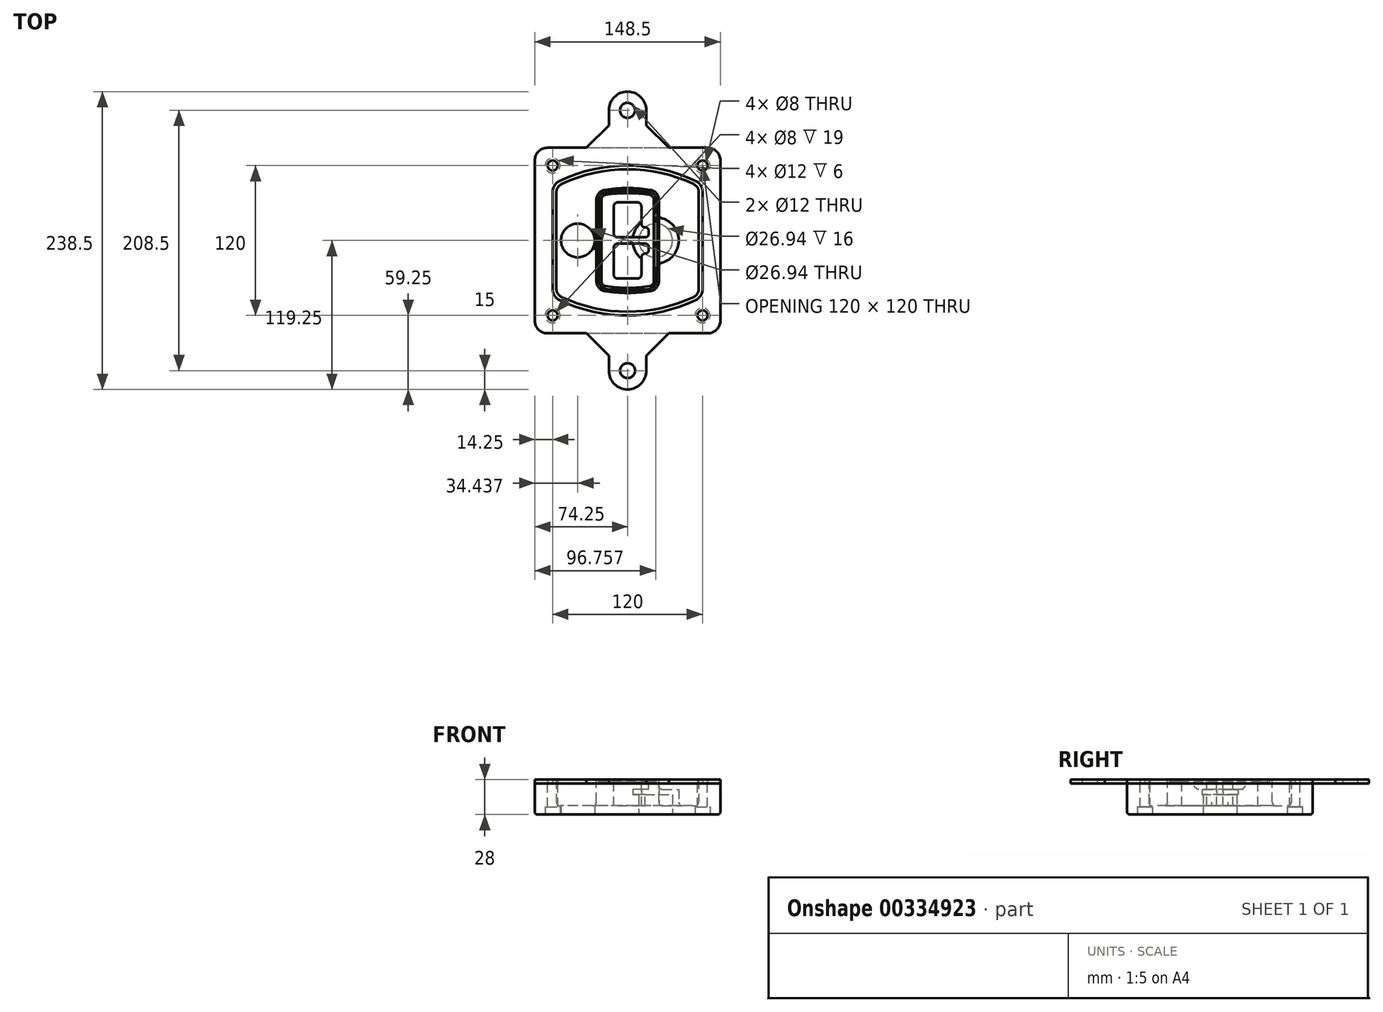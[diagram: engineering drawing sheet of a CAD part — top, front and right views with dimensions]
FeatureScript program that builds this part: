
annotation { "Feature Type Name" : "Feature", "Feature Type Description" : "" }
export const myFeature = defineFeature(function(context is Context, id is Id, definition is map)
    precondition{}
    {
        {
            var Q0;
            Q0=qCreatedBy(makeId("Top.planeOp"),FACE);
            var sketch = newSketch(context, id + "F0", { "sketchPlane" : qUnion([Q0])});
            skPoint(sketch, "E0.rect.middle", {"position": v(0, 0) * mm});
            skLineSegment(sketch, "E1.bottom", {"start": v(-64.25, -74.25) * mm, "end": v(64.25, -74.25) * mm});
            skLineSegment(sketch, "E1.top", {"start": v(-64.25, 74.25) * mm, "end": v(64.25, 74.25) * mm});
            skLineSegment(sketch, "E1.left", {"start": v(-74.25, -64.25) * mm, "end": v(-74.25, 64.25) * mm});
            skLineSegment(sketch, "E1.right", {"start": v(74.25, -64.25) * mm, "end": v(74.25, 64.25) * mm});
            skLineSegment(sketch, "E2", {"start": v(-74.25, 74.25) * mm, "end": v(74.25, -74.25) * mm, "construction": true});
            skLineSegment(sketch, "E3", {"start": v(74.25, 74.25) * mm, "end": v(-74.25, -74.25) * mm, "construction": true});
            skCircle(sketch, "E4", {"center": v(-60, 60) * mm, "radius": 4 * mm});
            skCircle(sketch, "E5", {"center": v(60, 60) * mm, "radius": 4 * mm});
            skCircle(sketch, "E6", {"center": v(60, -60) * mm, "radius": 4 * mm});
            skCircle(sketch, "E7", {"center": v(-60, -60) * mm, "radius": 4 * mm});
            skLineSegment(sketch, "E8", {"start": v(-60, 60) * mm, "end": v(60, 60) * mm, "construction": true});
            skLineSegment(sketch, "E9", {"start": v(60, 60) * mm, "end": v(60, -60) * mm, "construction": true});
            skLineSegment(sketch, "E10", {"start": v(60, -60) * mm, "end": v(-60, -60) * mm, "construction": true});
            skLineSegment(sketch, "E11", {"start": v(-60, -60) * mm, "end": v(-60, 60) * mm, "construction": true});
            skLineSegment(sketch, "E12", {"start": v(-60, 38.83) * mm, "end": v(-60, -38.83) * mm});
            skLineSegment(sketch, "E13", {"start": v(60, 38.83) * mm, "end": v(60, -38.83) * mm});
            skArc(sketch, "E14", {"start": v(54.26, 47.88) * mm, "mid": v(0, 60) * mm, "end": v(-54.26, 47.88) * mm});
            skArc(sketch, "E15", {"start": v(-54.26, -47.88) * mm, "mid": v(0, -60) * mm, "end": v(54.26, -47.88) * mm});
            skLineSegment(sketch, "E16", {"start": v(-60, 0) * mm, "end": v(60, 0) * mm, "construction": true});
            skPoint(sketch, "E17.visualSharp", {"position": v(-60, -45) * mm});
            skArc(sketch, "E17.filletArc", {"start": v(-60, -38.83) * mm, "mid": v(-58.44, -44.2) * mm, "end": v(-54.26, -47.88) * mm});
            skPoint(sketch, "E18.visualSharp", {"position": v(-60, 45) * mm});
            skArc(sketch, "E18.filletArc", {"start": v(-54.26, 47.88) * mm, "mid": v(-58.44, 44.2) * mm, "end": v(-60, 38.83) * mm});
            skPoint(sketch, "E19.visualSharp", {"position": v(60, 45) * mm});
            skArc(sketch, "E19.filletArc", {"start": v(60, 38.83) * mm, "mid": v(58.44, 44.2) * mm, "end": v(54.26, 47.88) * mm});
            skPoint(sketch, "E20.visualSharp", {"position": v(60, -45) * mm});
            skArc(sketch, "E20.filletArc", {"start": v(54.26, -47.88) * mm, "mid": v(58.44, -44.2) * mm, "end": v(60, -38.83) * mm});
            skPoint(sketch, "E21.visualSharp", {"position": v(-74.25, 74.25) * mm});
            skArc(sketch, "E21.filletArc", {"start": v(-64.25, 74.25) * mm, "mid": v(-71.32, 71.32) * mm, "end": v(-74.25, 64.25) * mm});
            skPoint(sketch, "E22.visualSharp", {"position": v(74.25, 74.25) * mm});
            skArc(sketch, "E22.filletArc", {"start": v(74.25, 64.25) * mm, "mid": v(71.32, 71.32) * mm, "end": v(64.25, 74.25) * mm});
            skPoint(sketch, "E23.visualSharp", {"position": v(74.25, -74.25) * mm});
            skArc(sketch, "E23.filletArc", {"start": v(64.25, -74.25) * mm, "mid": v(71.32, -71.32) * mm, "end": v(74.25, -64.25) * mm});
            skPoint(sketch, "E24.visualSharp", {"position": v(-74.25, -74.25) * mm});
            skArc(sketch, "E24.filletArc", {"start": v(-74.25, -64.25) * mm, "mid": v(-71.32, -71.32) * mm, "end": v(-64.25, -74.25) * mm});
            skArc(sketch, "E25.0", {"start": v(57, 38.83) * mm, "mid": v(55.9, 42.58) * mm, "end": v(52.98, 45.17) * mm});
            skLineSegment(sketch, "E25.1", {"start": v(57, 38.83) * mm, "end": v(57, -38.83) * mm});
            skArc(sketch, "E25.2", {"start": v(52.98, -45.17) * mm, "mid": v(55.9, -42.58) * mm, "end": v(57, -38.83) * mm});
            skArc(sketch, "E25.3", {"start": v(-52.98, -45.17) * mm, "mid": v(0, -57) * mm, "end": v(52.98, -45.17) * mm});
            skArc(sketch, "E25.4", {"start": v(-57, -38.83) * mm, "mid": v(-55.9, -42.58) * mm, "end": v(-52.98, -45.17) * mm});
            skArc(sketch, "E25.5", {"start": v(52.98, 45.17) * mm, "mid": v(0, 57) * mm, "end": v(-52.98, 45.17) * mm});
            skLineSegment(sketch, "E25.6", {"start": v(-57, 38.83) * mm, "end": v(-57, -38.83) * mm});
            skArc(sketch, "E25.7", {"start": v(-52.98, 45.17) * mm, "mid": v(-55.9, 42.58) * mm, "end": v(-57, 38.83) * mm});
            skArc(sketch, "E26.0", {"start": v(-55.96, 51.5) * mm, "mid": v(-61.82, 46.33) * mm, "end": v(-64, 38.83) * mm});
            skArc(sketch, "E26.1", {"start": v(55.96, 51.5) * mm, "mid": v(0, 64) * mm, "end": v(-55.96, 51.5) * mm});
            skArc(sketch, "E26.2", {"start": v(64, 38.83) * mm, "mid": v(61.82, 46.33) * mm, "end": v(55.96, 51.5) * mm});
            skLineSegment(sketch, "E26.3", {"start": v(64, 38.83) * mm, "end": v(64, -38.83) * mm});
            skArc(sketch, "E26.4", {"start": v(55.96, -51.5) * mm, "mid": v(61.82, -46.33) * mm, "end": v(64, -38.83) * mm});
            skLineSegment(sketch, "E26.5", {"start": v(-64, 38.83) * mm, "end": v(-64, -38.83) * mm});
            skArc(sketch, "E26.6", {"start": v(-55.96, -51.5) * mm, "mid": v(0, -64) * mm, "end": v(55.96, -51.5) * mm});
            skArc(sketch, "E26.7", {"start": v(-64, -38.83) * mm, "mid": v(-61.82, -46.33) * mm, "end": v(-55.96, -51.5) * mm});
            skSolve(sketch);
        }
        {
            var Q0;
            Q0=makeQuery(id+"F0.imprint","IMPRINT",FACE,{"disambiguationData":[TD([[makeQuery(id+"F0.imprint","IMPRINT",EDGE,{"derivedFrom":sQuery(id+"F0.wireOp",EDGE,"E1.bottom")}),1.0]])]});
            var Q1;
            Q1=makeQuery(id+"F0.imprint","IMPRINT",FACE,{"disambiguationData":[TD([[makeQuery(id+"F0.imprint","IMPRINT",EDGE,{"derivedFrom":sQuery(id+"F0.wireOp",EDGE,"E12")}),1.0]])]});
            var Q2;
            Q2=makeQuery(id+"F0.imprint","IMPRINT",FACE,{"disambiguationData":[TD([[makeQuery(id+"F0.imprint","IMPRINT",EDGE,{"derivedFrom":sQuery(id+"F0.wireOp",EDGE,"E25.0")}),1.0]])]});
            var Q3;
            Q3=makeQuery(id+"F0.imprint","IMPRINT",FACE,{"disambiguationData":[TD([[makeQuery(id+"F0.imprint","IMPRINT",EDGE,{"derivedFrom":sQuery(id+"F0.wireOp",EDGE,"E12")}),-1.0]])]});
            extrude(context, id + "F1", {"entities" : qUnion([Q0, Q1, Q2, Q3]), "oppositeDirection" : true, "depth" : 25 * mm});
        }
        {
            var Q0;
            Q0=makeQuery(id+"F0.imprint","IMPRINT",FACE,{"disambiguationData":[TD([[makeQuery(id+"F0.imprint","IMPRINT",EDGE,{"derivedFrom":sQuery(id+"F0.wireOp",EDGE,"E12")}),1.0]])]});
            extrude(context, id + "F2", {"entities" : qUnion([Q0]), "operationType" : NewBodyOperationType.ADD, "depth" : 3 * mm});
        }
        {
            var Q0;
            Q0=makeQuery(id+"F0.imprint","IMPRINT",FACE,{"disambiguationData":[TD([[makeQuery(id+"F0.imprint","IMPRINT",EDGE,{"derivedFrom":sQuery(id+"F0.wireOp",EDGE,"E25.0")}),1.0]])]});
            extrude(context, id + "F3", {"entities" : qUnion([Q0]), "operationType" : NewBodyOperationType.REMOVE, "oppositeDirection" : true, "depth" : 18 * mm});
        }
        {
            var Q0;
            Q0=makeQuery(id+"F2.opExtrude","CAP_FACE",FACE,{"disambiguationData":[OSD([sQuery(id+"F0.wireOp",EDGE,"E12"),sQuery(id+"F0.wireOp",EDGE,"E13"),sQuery(id+"F0.wireOp",EDGE,"E14"),sQuery(id+"F0.wireOp",EDGE,"E15"),sQuery(id+"F0.wireOp",EDGE,"E17.filletArc"),sQuery(id+"F0.wireOp",EDGE,"E18.filletArc"),sQuery(id+"F0.wireOp",EDGE,"E19.filletArc"),sQuery(id+"F0.wireOp",EDGE,"E20.filletArc"),sQuery(id+"F0.wireOp",EDGE,"E25.0"),sQuery(id+"F0.wireOp",EDGE,"E25.1"),sQuery(id+"F0.wireOp",EDGE,"E25.2"),sQuery(id+"F0.wireOp",EDGE,"E25.3"),sQuery(id+"F0.wireOp",EDGE,"E25.4"),sQuery(id+"F0.wireOp",EDGE,"E25.5"),sQuery(id+"F0.wireOp",EDGE,"E25.6"),sQuery(id+"F0.wireOp",EDGE,"E25.7")])],"isStart":false});
            var sketch = newSketch(context, id + "F4", { "sketchPlane" : qUnion([Q0])});
            skArc(sketch, "E27.0", {"start": v(-18.34, -40.45) * mm, "mid": v(0, -42) * mm, "end": v(18.34, -40.45) * mm});
            skArc(sketch, "E28.0", {"start": v(18.34, 40.45) * mm, "mid": v(0, 42) * mm, "end": v(-18.34, 40.45) * mm});
            skLineSegment(sketch, "E29", {"start": v(-25, 32.57) * mm, "end": v(-25, -32.57) * mm});
            skLineSegment(sketch, "E30", {"start": v(25, 32.57) * mm, "end": v(25, -32.57) * mm});
            skLineSegment(sketch, "E31", {"start": v(-25, 39.1) * mm, "end": v(25, 39.1) * mm, "construction": true});
            skLineSegment(sketch, "E32", {"start": v(-25, -39.1) * mm, "end": v(25, -39.1) * mm, "construction": true});
            skPoint(sketch, "E33.visualSharp", {"position": v(-25, 39.1) * mm});
            skArc(sketch, "E33.filletArc", {"start": v(-18.34, 40.45) * mm, "mid": v(-23.11, 37.73) * mm, "end": v(-25, 32.57) * mm});
            skPoint(sketch, "E34.visualSharp", {"position": v(25, 39.1) * mm});
            skArc(sketch, "E34.filletArc", {"start": v(25, 32.57) * mm, "mid": v(23.11, 37.73) * mm, "end": v(18.34, 40.45) * mm});
            skPoint(sketch, "E35.visualSharp", {"position": v(25, -39.1) * mm});
            skArc(sketch, "E35.filletArc", {"start": v(18.34, -40.45) * mm, "mid": v(23.11, -37.73) * mm, "end": v(25, -32.57) * mm});
            skPoint(sketch, "E36.visualSharp", {"position": v(-25, -39.1) * mm});
            skArc(sketch, "E36.filletArc", {"start": v(-25, -32.57) * mm, "mid": v(-23.11, -37.73) * mm, "end": v(-18.34, -40.45) * mm});
            skArc(sketch, "E37.0", {"start": v(52.98, 45.17) * mm, "mid": v(0, 57) * mm, "end": v(-52.98, 45.17) * mm});
            skArc(sketch, "E37.1", {"start": v(-52.98, 45.17) * mm, "mid": v(-55.9, 42.58) * mm, "end": v(-57, 38.83) * mm});
            skLineSegment(sketch, "E37.2", {"start": v(-57, 38.83) * mm, "end": v(-57, -38.83) * mm});
            skArc(sketch, "E37.3", {"start": v(-57, -38.83) * mm, "mid": v(-55.9, -42.58) * mm, "end": v(-52.98, -45.17) * mm});
            skArc(sketch, "E37.4", {"start": v(-52.98, -45.17) * mm, "mid": v(0, -57) * mm, "end": v(52.98, -45.17) * mm});
            skArc(sketch, "E37.5", {"start": v(52.98, -45.17) * mm, "mid": v(55.9, -42.58) * mm, "end": v(57, -38.83) * mm});
            skLineSegment(sketch, "E37.6", {"start": v(57, 38.83) * mm, "end": v(57, -38.83) * mm});
            skArc(sketch, "E37.7", {"start": v(57, 38.83) * mm, "mid": v(55.9, 42.58) * mm, "end": v(52.98, 45.17) * mm});
            skLineSegment(sketch, "E38.0", {"start": v(23, 32.57) * mm, "end": v(23, -32.57) * mm});
            skArc(sketch, "E38.1", {"start": v(18, -38.48) * mm, "mid": v(21.58, -36.44) * mm, "end": v(23, -32.57) * mm});
            skArc(sketch, "E38.2", {"start": v(-18, -38.48) * mm, "mid": v(0, -40) * mm, "end": v(18, -38.48) * mm});
            skArc(sketch, "E38.3", {"start": v(-23, -32.57) * mm, "mid": v(-21.58, -36.44) * mm, "end": v(-18, -38.48) * mm});
            skLineSegment(sketch, "E38.4", {"start": v(-23, 32.57) * mm, "end": v(-23, -32.57) * mm});
            skArc(sketch, "E38.5", {"start": v(23, 32.57) * mm, "mid": v(21.58, 36.44) * mm, "end": v(18, 38.48) * mm});
            skArc(sketch, "E38.6", {"start": v(-18, 38.48) * mm, "mid": v(-21.58, 36.44) * mm, "end": v(-23, 32.57) * mm});
            skArc(sketch, "E38.7", {"start": v(18, 38.48) * mm, "mid": v(0, 40) * mm, "end": v(-18, 38.48) * mm});
            skArc(sketch, "E39.0", {"start": v(21, 32.57) * mm, "mid": v(20.06, 35.15) * mm, "end": v(17.67, 36.5) * mm});
            skLineSegment(sketch, "E39.1", {"start": v(21, 32.57) * mm, "end": v(21, -32.57) * mm});
            skArc(sketch, "E39.2", {"start": v(17.67, -36.5) * mm, "mid": v(20.06, -35.15) * mm, "end": v(21, -32.57) * mm});
            skArc(sketch, "E39.3", {"start": v(-17.67, -36.5) * mm, "mid": v(0, -38) * mm, "end": v(17.67, -36.5) * mm});
            skArc(sketch, "E39.4", {"start": v(-21, -32.57) * mm, "mid": v(-20.06, -35.15) * mm, "end": v(-17.67, -36.5) * mm});
            skArc(sketch, "E39.5", {"start": v(17.67, 36.5) * mm, "mid": v(0, 38) * mm, "end": v(-17.67, 36.5) * mm});
            skLineSegment(sketch, "E39.6", {"start": v(-21, 32.57) * mm, "end": v(-21, -32.57) * mm});
            skArc(sketch, "E39.7", {"start": v(-17.67, 36.5) * mm, "mid": v(-20.06, 35.15) * mm, "end": v(-21, 32.57) * mm});
            skLineSegment(sketch, "E40", {"start": v(-25, 0) * mm, "end": v(25, 0) * mm, "construction": true});
            skLineSegment(sketch, "E41", {"start": v(-11, 5.5) * mm, "end": v(-11, 27.5) * mm});
            skLineSegment(sketch, "E42", {"start": v(-8, 30.5) * mm, "end": v(8, 30.5) * mm});
            skLineSegment(sketch, "E43", {"start": v(11, 27.5) * mm, "end": v(11, 13.5) * mm});
            skLineSegment(sketch, "E44", {"start": v(14, 10.5) * mm, "end": v(14, 10.5) * mm});
            skLineSegment(sketch, "E45", {"start": v(17, 7.5) * mm, "end": v(17, 5.5) * mm});
            skLineSegment(sketch, "E46", {"start": v(14, 2.5) * mm, "end": v(-8, 2.5) * mm});
            skPoint(sketch, "E47.visualSharp", {"position": v(-11, 30.5) * mm});
            skArc(sketch, "E47.filletArc", {"start": v(-8, 30.5) * mm, "mid": v(-10.12, 29.62) * mm, "end": v(-11, 27.5) * mm});
            skPoint(sketch, "E48.visualSharp", {"position": v(11, 30.5) * mm});
            skArc(sketch, "E48.filletArc", {"start": v(11, 27.5) * mm, "mid": v(10.12, 29.62) * mm, "end": v(8, 30.5) * mm});
            skPoint(sketch, "E49.visualSharp", {"position": v(11, 10.5) * mm});
            skArc(sketch, "E49.filletArc", {"start": v(11, 13.5) * mm, "mid": v(11.88, 11.38) * mm, "end": v(14, 10.5) * mm});
            skPoint(sketch, "E50.visualSharp", {"position": v(17, 10.5) * mm});
            skArc(sketch, "E50.filletArc", {"start": v(17, 7.5) * mm, "mid": v(16.12, 9.62) * mm, "end": v(14, 10.5) * mm});
            skPoint(sketch, "E51.visualSharp", {"position": v(17, 2.5) * mm});
            skArc(sketch, "E51.filletArc", {"start": v(14, 2.5) * mm, "mid": v(16.12, 3.38) * mm, "end": v(17, 5.5) * mm});
            skPoint(sketch, "E52.visualSharp", {"position": v(-11, 2.5) * mm});
            skArc(sketch, "E52.filletArc", {"start": v(-11, 5.5) * mm, "mid": v(-10.12, 3.38) * mm, "end": v(-8, 2.5) * mm});
            skLineSegment(sketch, "E53.0.MirrorCS", {"start": v(14, -2.5) * mm, "end": v(-8, -2.5) * mm});
            skArc(sketch, "E54.0.MirrorCS", {"start": v(-11, -5.5) * mm, "mid": v(-10.12, -3.38) * mm, "end": v(-8, -2.5) * mm});
            skLineSegment(sketch, "E55.0.MirrorCS", {"start": v(-11, -5.5) * mm, "end": v(-11, -27.5) * mm});
            skArc(sketch, "E56.0.MirrorCS", {"start": v(-8, -30.5) * mm, "mid": v(-10.12, -29.62) * mm, "end": v(-11, -27.5) * mm});
            skLineSegment(sketch, "E57.0.MirrorCS", {"start": v(-8, -30.5) * mm, "end": v(8, -30.5) * mm});
            skArc(sketch, "E58.0.MirrorCS", {"start": v(11, -27.5) * mm, "mid": v(10.12, -29.62) * mm, "end": v(8, -30.5) * mm});
            skLineSegment(sketch, "E59.0.MirrorCS", {"start": v(11, -27.5) * mm, "end": v(11, -13.5) * mm});
            skArc(sketch, "E60.0.MirrorCS", {"start": v(11, -13.5) * mm, "mid": v(11.88, -11.38) * mm, "end": v(14, -10.5) * mm});
            skArc(sketch, "E61.0.MirrorCS", {"start": v(17, -7.5) * mm, "mid": v(16.12, -9.62) * mm, "end": v(14, -10.5) * mm});
            skLineSegment(sketch, "E62.0.MirrorCS", {"start": v(17, -7.5) * mm, "end": v(17, -5.5) * mm});
            skArc(sketch, "E63.0.MirrorCS", {"start": v(14, -2.5) * mm, "mid": v(16.12, -3.38) * mm, "end": v(17, -5.5) * mm});
            skSolve(sketch);
        }
        {
            var Q0;
            Q0=makeQuery(id+"F4.imprint","IMPRINT",FACE,{"disambiguationData":[TD([[makeQuery(id+"F4.imprint","IMPRINT",EDGE,{"derivedFrom":sQuery(id+"F4.wireOp",EDGE,"E27.0")}),1.0]])]});
            var Q1;
            Q1=makeQuery(id+"F4.imprint","IMPRINT",FACE,{"disambiguationData":[TD([[makeQuery(id+"F4.imprint","IMPRINT",EDGE,{"derivedFrom":sQuery(id+"F4.wireOp",EDGE,"E38.0")}),-1.0]])]});
            var Q2;
            Q2=makeQuery(id+"F4.imprint","IMPRINT",FACE,{"disambiguationData":[TD([[makeQuery(id+"F4.imprint","IMPRINT",EDGE,{"derivedFrom":sQuery(id+"F4.wireOp",EDGE,"E39.0")}),1.0]])]});
            extrude(context, id + "F5", {"entities" : qUnion([Q0, Q1, Q2]), "operationType" : NewBodyOperationType.ADD, "endBound" : BoundingType.UP_TO_NEXT, "oppositeDirection" : true, "depth" : 25 * mm});
        }
        {
            var Q0;
            Q0=makeQuery(id+"F4.imprint","IMPRINT",FACE,{"disambiguationData":[TD([[makeQuery(id+"F4.imprint","IMPRINT",EDGE,{"derivedFrom":sQuery(id+"F4.wireOp",EDGE,"E38.0")}),-1.0]])]});
            extrude(context, id + "F6", {"entities" : qUnion([Q0]), "operationType" : NewBodyOperationType.REMOVE, "oppositeDirection" : true, "depth" : 2 * mm});
        }
        {
            var Q0;
            Q0=makeQuery(id+"F1.opExtrude","CAP_FACE",FACE,{"disambiguationData":[OSD([sQuery(id+"F0.wireOp",EDGE,"E1.bottom"),sQuery(id+"F0.wireOp",EDGE,"E1.top"),sQuery(id+"F0.wireOp",EDGE,"E1.left"),sQuery(id+"F0.wireOp",EDGE,"E1.right"),sQuery(id+"F0.wireOp",EDGE,"E4"),sQuery(id+"F0.wireOp",EDGE,"E5"),sQuery(id+"F0.wireOp",EDGE,"E6"),sQuery(id+"F0.wireOp",EDGE,"E7"),sQuery(id+"F0.wireOp",EDGE,"E21.filletArc"),sQuery(id+"F0.wireOp",EDGE,"E22.filletArc"),sQuery(id+"F0.wireOp",EDGE,"E23.filletArc"),sQuery(id+"F0.wireOp",EDGE,"E24.filletArc")])],"isStart":false});
            var sketch = newSketch(context, id + "F7", { "sketchPlane" : qUnion([Q0])});
            skCircle(sketch, "E64", {"center": v(22.5, 0) * mm, "radius": 13.47 * mm});
            skCircle(sketch, "E65", {"center": v(-39.81, 0) * mm, "radius": 13.47 * mm});
            skLineSegment(sketch, "E66", {"start": v(74.25, 0) * mm, "end": v(-74.25, 0) * mm});
            skCircle(sketch, "E67", {"center": v(22.5, 0) * mm, "radius": 18.47 * mm});
            skCircle(sketch, "E68", {"center": v(60, -60) * mm, "radius": 6 * mm});
            skCircle(sketch, "E69", {"center": v(-60, -60) * mm, "radius": 6 * mm});
            skCircle(sketch, "E70", {"center": v(-60, 60) * mm, "radius": 6 * mm});
            skCircle(sketch, "E71", {"center": v(60, 60) * mm, "radius": 6 * mm});
            skSolve(sketch);
        }
        {
            var Q0;
            {var subQ1=sQuery(id+"F7.wireOp",EDGE,"E66");var subQ4=sQuery(id+"F7.wireOp",EDGE,"E64");var subQ6=makeQuery(id+"F7.imprint","INTERSECT",VERTEX,{"disambiguationData":[OD(0.0)],"derivedFrom":[subQ4,subQ1]});Q0=makeQuery(id+"F7.imprint","IMPRINT",FACE,{"disambiguationData":[TD([[makeQuery(id+"F7.imprint","IMPRINT",EDGE,{"disambiguationData":[TD([[subQ6,-1.0]])],"derivedFrom":subQ4}),-1.0]])]});}
            var Q1;
            {var subQ0=sQuery(id+"F7.wireOp",EDGE,"E66");var subQ1=sQuery(id+"F7.wireOp",EDGE,"E64");var subQ3=makeQuery(id+"F7.imprint","INTERSECT",VERTEX,{"disambiguationData":[OD(0.0)],"derivedFrom":[subQ1,subQ0]});Q1=makeQuery(id+"F7.imprint","IMPRINT",FACE,{"disambiguationData":[TD([[makeQuery(id+"F7.imprint","IMPRINT",EDGE,{"disambiguationData":[TD([[subQ3,-1.0]])],"derivedFrom":subQ1}),1.0]])]});}
            var Q2;
            {var subQ0=sQuery(id+"F7.wireOp",EDGE,"E66");var subQ1=sQuery(id+"F7.wireOp",EDGE,"E64");var subQ3=makeQuery(id+"F7.imprint","INTERSECT",VERTEX,{"disambiguationData":[OD(0.0)],"derivedFrom":[subQ1,subQ0]});Q2=makeQuery(id+"F7.imprint","IMPRINT",FACE,{"disambiguationData":[TD([[makeQuery(id+"F7.imprint","IMPRINT",EDGE,{"disambiguationData":[TD([[subQ3,1.0]])],"derivedFrom":subQ1}),1.0]])]});}
            var Q3;
            {var subQ1=sQuery(id+"F7.wireOp",EDGE,"E66");var subQ4=sQuery(id+"F7.wireOp",EDGE,"E64");var subQ6=makeQuery(id+"F7.imprint","INTERSECT",VERTEX,{"disambiguationData":[OD(0.0)],"derivedFrom":[subQ4,subQ1]});Q3=makeQuery(id+"F7.imprint","IMPRINT",FACE,{"disambiguationData":[TD([[makeQuery(id+"F7.imprint","IMPRINT",EDGE,{"disambiguationData":[TD([[subQ6,1.0]])],"derivedFrom":subQ4}),-1.0]])]});}
            extrude(context, id + "F8", {"entities" : qUnion([Q0, Q1, Q2, Q3]), "operationType" : NewBodyOperationType.ADD, "oppositeDirection" : true, "depth" : 20 * mm});
        }
        {
            var Q0;
            {var subQ0=sQuery(id+"F7.wireOp",EDGE,"E66");var subQ1=sQuery(id+"F7.wireOp",EDGE,"E64");var subQ3=makeQuery(id+"F7.imprint","INTERSECT",VERTEX,{"disambiguationData":[OD(0.0)],"derivedFrom":[subQ1,subQ0]});Q0=makeQuery(id+"F7.imprint","IMPRINT",FACE,{"disambiguationData":[TD([[makeQuery(id+"F7.imprint","IMPRINT",EDGE,{"disambiguationData":[TD([[subQ3,-1.0]])],"derivedFrom":subQ1}),1.0]])]});}
            var Q1;
            {var subQ0=sQuery(id+"F7.wireOp",EDGE,"E66");var subQ1=sQuery(id+"F7.wireOp",EDGE,"E64");var subQ3=makeQuery(id+"F7.imprint","INTERSECT",VERTEX,{"disambiguationData":[OD(0.0)],"derivedFrom":[subQ1,subQ0]});Q1=makeQuery(id+"F7.imprint","IMPRINT",FACE,{"disambiguationData":[TD([[makeQuery(id+"F7.imprint","IMPRINT",EDGE,{"disambiguationData":[TD([[subQ3,1.0]])],"derivedFrom":subQ1}),1.0]])]});}
            extrude(context, id + "F9", {"entities" : qUnion([Q0, Q1]), "operationType" : NewBodyOperationType.REMOVE, "oppositeDirection" : true, "depth" : 16 * mm});
        }
        {
            var Q0;
            {var subQ0=sQuery(id+"F7.wireOp",EDGE,"E66");var subQ1=sQuery(id+"F7.wireOp",EDGE,"E65");var subQ3=makeQuery(id+"F7.imprint","INTERSECT",VERTEX,{"disambiguationData":[OD(0.0)],"derivedFrom":[subQ1,subQ0]});Q0=makeQuery(id+"F7.imprint","IMPRINT",FACE,{"disambiguationData":[TD([[makeQuery(id+"F7.imprint","IMPRINT",EDGE,{"disambiguationData":[TD([[subQ3,-1.0]])],"derivedFrom":subQ1}),1.0]])]});}
            var Q1;
            {var subQ0=sQuery(id+"F7.wireOp",EDGE,"E66");var subQ1=sQuery(id+"F7.wireOp",EDGE,"E65");var subQ3=makeQuery(id+"F7.imprint","INTERSECT",VERTEX,{"disambiguationData":[OD(0.0)],"derivedFrom":[subQ1,subQ0]});Q1=makeQuery(id+"F7.imprint","IMPRINT",FACE,{"disambiguationData":[TD([[makeQuery(id+"F7.imprint","IMPRINT",EDGE,{"disambiguationData":[TD([[subQ3,1.0]])],"derivedFrom":subQ1}),1.0]])]});}
            extrude(context, id + "F10", {"entities" : qUnion([Q0, Q1]), "operationType" : NewBodyOperationType.REMOVE, "oppositeDirection" : true, "depth" : 25 * mm});
        }
        {
            var Q0;
            Q0=makeQuery(id+"F7.imprint","IMPRINT",FACE,{"disambiguationData":[TD([[makeQuery(id+"F7.imprint","IMPRINT",EDGE,{"derivedFrom":sQuery(id+"F7.wireOp",EDGE,"E68")}),1.0]])]});
            var Q1;
            Q1=makeQuery(id+"F7.imprint","IMPRINT",FACE,{"disambiguationData":[TD([[makeQuery(id+"F7.imprint","IMPRINT",EDGE,{"derivedFrom":makeQuery(id+"F1.opExtrude","CAP_EDGE",EDGE,{"disambiguationData":[OSD([sQuery(id+"F0.wireOp",EDGE,"E5")])],"isStart":false})}),-1.0]])]});
            var Q2;
            Q2=makeQuery(id+"F7.imprint","IMPRINT",FACE,{"disambiguationData":[TD([[makeQuery(id+"F7.imprint","IMPRINT",EDGE,{"derivedFrom":sQuery(id+"F7.wireOp",EDGE,"E69")}),1.0]])]});
            var Q3;
            Q3=makeQuery(id+"F7.imprint","IMPRINT",FACE,{"disambiguationData":[TD([[makeQuery(id+"F7.imprint","IMPRINT",EDGE,{"derivedFrom":makeQuery(id+"F1.opExtrude","CAP_EDGE",EDGE,{"disambiguationData":[OSD([sQuery(id+"F0.wireOp",EDGE,"E4")])],"isStart":false})}),-1.0]])]});
            var Q4;
            Q4=makeQuery(id+"F7.imprint","IMPRINT",FACE,{"disambiguationData":[TD([[makeQuery(id+"F7.imprint","IMPRINT",EDGE,{"derivedFrom":sQuery(id+"F7.wireOp",EDGE,"E70")}),1.0]])]});
            var Q5;
            Q5=makeQuery(id+"F7.imprint","IMPRINT",FACE,{"disambiguationData":[TD([[makeQuery(id+"F7.imprint","IMPRINT",EDGE,{"derivedFrom":makeQuery(id+"F1.opExtrude","CAP_EDGE",EDGE,{"disambiguationData":[OSD([sQuery(id+"F0.wireOp",EDGE,"E7")])],"isStart":false})}),-1.0]])]});
            var Q6;
            Q6=makeQuery(id+"F7.imprint","IMPRINT",FACE,{"disambiguationData":[TD([[makeQuery(id+"F7.imprint","IMPRINT",EDGE,{"derivedFrom":sQuery(id+"F7.wireOp",EDGE,"E71")}),1.0]])]});
            var Q7;
            Q7=makeQuery(id+"F7.imprint","IMPRINT",FACE,{"disambiguationData":[TD([[makeQuery(id+"F7.imprint","IMPRINT",EDGE,{"derivedFrom":makeQuery(id+"F1.opExtrude","CAP_EDGE",EDGE,{"disambiguationData":[OSD([sQuery(id+"F0.wireOp",EDGE,"E6")])],"isStart":false})}),-1.0]])]});
            extrude(context, id + "F11", {"entities" : qUnion([Q0, Q1, Q2, Q3, Q4, Q5, Q6, Q7]), "operationType" : NewBodyOperationType.REMOVE, "oppositeDirection" : true, "depth" : 6 * mm});
        }
        {
            var Q0;
            Q0=makeQuery(id+"F9.boolean.opBoolean","COPY",FACE,{"derivedFrom":makeQuery(id+"F9.opExtrude","CAP_FACE",FACE,{"disambiguationData":[OSD([sQuery(id+"F7.wireOp",EDGE,"E64")])],"isStart":false})});
            var sketch = newSketch(context, id + "F12", { "sketchPlane" : qUnion([Q0])});
            skArc(sketch, "E72.0", {"start": v(11, 14.45) * mm, "mid": v(6.45, 9.13) * mm, "end": v(4.2, 2.5) * mm});
            skArc(sketch, "E72.1", {"start": v(4.2, -2.5) * mm, "mid": v(6.45, -9.13) * mm, "end": v(11, -14.45) * mm});
            skLineSegment(sketch, "E73", {"start": v(4.2, -2.5) * mm, "end": v(14, -2.5) * mm});
            skLineSegment(sketch, "E74.0", {"start": v(14, 2.5) * mm, "end": v(4.2, 2.5) * mm});
            skArc(sketch, "E74.1", {"start": v(14, 2.5) * mm, "mid": v(16.12, 3.38) * mm, "end": v(17, 5.5) * mm});
            skLineSegment(sketch, "E74.2", {"start": v(17, 7.5) * mm, "end": v(17, 5.5) * mm});
            skArc(sketch, "E74.3", {"start": v(17, 7.5) * mm, "mid": v(16.12, 9.62) * mm, "end": v(14, 10.5) * mm});
            skArc(sketch, "E74.4", {"start": v(11, 13.5) * mm, "mid": v(11.88, 11.38) * mm, "end": v(14, 10.5) * mm});
            skLineSegment(sketch, "E74.5", {"start": v(11, 14.45) * mm, "end": v(11, 13.5) * mm});
            skLineSegment(sketch, "E74.7", {"start": v(14, -2.5) * mm, "end": v(4.2, -2.5) * mm});
            skArc(sketch, "E74.8", {"start": v(14, -2.5) * mm, "mid": v(16.12, -3.38) * mm, "end": v(17, -5.5) * mm});
            skLineSegment(sketch, "E74.9", {"start": v(17, -7.5) * mm, "end": v(17, -5.5) * mm});
            skArc(sketch, "E74.10", {"start": v(17, -7.5) * mm, "mid": v(16.12, -9.62) * mm, "end": v(14, -10.5) * mm});
            skArc(sketch, "E74.11", {"start": v(11, -13.5) * mm, "mid": v(11.88, -11.38) * mm, "end": v(14, -10.5) * mm});
            skLineSegment(sketch, "E74.12", {"start": v(11, -14.45) * mm, "end": v(11, -13.5) * mm});
            skPoint(sketch, "E75.orphan", {"position": v(11, -27.5) * mm});
            skPoint(sketch, "E76.orphan", {"position": v(-8, -2.5) * mm});
            skPoint(sketch, "E77.orphan", {"position": v(-8, 2.5) * mm});
            skPoint(sketch, "E78.orphan", {"position": v(11, 27.5) * mm});
            skSolve(sketch);
        }
        {
            var Q0;
            {var subQ7=sQuery(id+"F12.wireOp",EDGE,"E72.0");var subQ14=sQuery(id+"F12.wireOp",EDGE,"E72.1");var subQ16=sQuery(id+"F12.wireOp",EDGE,"E74.1");var subQ18=sQuery(id+"F12.wireOp",EDGE,"E74.8");Q0=qUnion([makeQuery(id+"F12.imprint","IMPRINT",FACE,{"disambiguationData":[TD([[makeQuery(id+"F12.imprint","IMPRINT",EDGE,{"derivedFrom":subQ7}),1.0]])]}),makeQuery(id+"F12.imprint","IMPRINT",FACE,{"disambiguationData":[TD([[makeQuery(id+"F12.imprint","IMPRINT",EDGE,{"derivedFrom":subQ14}),1.0]])]}),makeQuery(id+"F12.imprint","IMPRINT",FACE,{"disambiguationData":[TD([[makeQuery(id+"F12.imprint","IMPRINT",EDGE,{"derivedFrom":subQ16}),1.0]])]}),makeQuery(id+"F12.imprint","IMPRINT",FACE,{"disambiguationData":[TD([[makeQuery(id+"F12.imprint","IMPRINT",EDGE,{"derivedFrom":subQ18}),-1.0]])]})]);}
            var Q1;
            Q1=makeQuery(id+"F5.boolean.opBoolean","SPLIT",FACE,{"disambiguationData":[TD([makeQuery(id+"F5.opExtrude","SWEPT_FACE",FACE,{"disambiguationData":[OSD([sQuery(id+"F4.wireOp",EDGE,"E41")])]})])],"derivedFrom":makeQuery(id+"F3.boolean.opBoolean","COPY",FACE,{"derivedFrom":makeQuery(id+"F3.opExtrude","CAP_FACE",FACE,{"disambiguationData":[OSD([sQuery(id+"F0.wireOp",EDGE,"E25.0"),sQuery(id+"F0.wireOp",EDGE,"E25.1"),sQuery(id+"F0.wireOp",EDGE,"E25.2"),sQuery(id+"F0.wireOp",EDGE,"E25.3"),sQuery(id+"F0.wireOp",EDGE,"E25.4"),sQuery(id+"F0.wireOp",EDGE,"E25.5"),sQuery(id+"F0.wireOp",EDGE,"E25.6"),sQuery(id+"F0.wireOp",EDGE,"E25.7")])],"isStart":false})})});
            extrude(context, id + "F13", {"entities" : qUnion([Q0]), "operationType" : NewBodyOperationType.REMOVE, "endBound" : BoundingType.UP_TO_SURFACE, "endBoundEntityFace" : qUnion([Q1]), "depth" : 25 * mm});
        }
        {
            var Q0;
            Q0=makeQuery(id+"F3.boolean.opBoolean","COPY",EDGE,{"derivedFrom":makeQuery(id+"F3.opExtrude","CAP_EDGE",EDGE,{"disambiguationData":[OSD([sQuery(id+"F0.wireOp",EDGE,"E25.6")])],"isStart":false})});
            var Q1;
            Q1=makeQuery(id+"F8.boolean.opBoolean","INTERSECT",EDGE,{"derivedFrom":[makeQuery(id+"F5.opExtrude","SWEPT_FACE",FACE,{"disambiguationData":[OSD([sQuery(id+"F4.wireOp",EDGE,"E30")])]}),makeQuery(id+"F8.opExtrude","CAP_FACE",FACE,{"disambiguationData":[OSD([sQuery(id+"F7.wireOp",EDGE,"E67")])],"isStart":false})]});
            var Q2;
            Q2=makeQuery(id+"F8.boolean.opBoolean","INTERSECT",EDGE,{"disambiguationData":[OD(1.0)],"derivedFrom":[makeQuery(id+"F5.opExtrude","SWEPT_FACE",FACE,{"disambiguationData":[OSD([sQuery(id+"F4.wireOp",EDGE,"E30")])]}),makeQuery(id+"F8.opExtrude","SWEPT_FACE",FACE,{"disambiguationData":[OSD([sQuery(id+"F7.wireOp",EDGE,"E67")])]})]});
            var Q3;
            {var subQ0=sQuery(id+"F4.wireOp",EDGE,"E30");Q3=makeQuery(id+"F8.boolean.opBoolean","SPLIT",EDGE,{"disambiguationData":[TD([makeQuery(id+"F5.opExtrude","SWEPT_FACE",FACE,{"disambiguationData":[OSD([sQuery(id+"F4.wireOp",EDGE,"E35.filletArc")])]})])],"derivedFrom":makeQuery(id+"F5.opExtrude","CAP_EDGE",EDGE,{"disambiguationData":[OSD([subQ0])],"isStart":false})});}
            var Q4;
            {var subQ0=sQuery(id+"F0.wireOp",EDGE,"E25.7");var subQ1=sQuery(id+"F0.wireOp",EDGE,"E25.1");var subQ2=sQuery(id+"F0.wireOp",EDGE,"E25.6");var subQ3=sQuery(id+"F0.wireOp",EDGE,"E25.5");var subQ4=sQuery(id+"F0.wireOp",EDGE,"E25.4");var subQ5=sQuery(id+"F0.wireOp",EDGE,"E25.0");var subQ6=sQuery(id+"F0.wireOp",EDGE,"E25.2");var subQ7=sQuery(id+"F0.wireOp",EDGE,"E25.3");Q4=makeQuery(id+"F8.boolean.opBoolean","INTERSECT",EDGE,{"derivedFrom":[makeQuery(id+"F5.boolean.opBoolean","SPLIT",FACE,{"disambiguationData":[TD([makeQuery(id+"F2.opExtrude","SWEPT_FACE",FACE,{"disambiguationData":[OSD([subQ5])]})])],"derivedFrom":makeQuery(id+"F3.boolean.opBoolean","COPY",FACE,{"derivedFrom":makeQuery(id+"F3.opExtrude","CAP_FACE",FACE,{"disambiguationData":[OSD([subQ5,subQ1,subQ6,subQ7,subQ4,subQ3,subQ2,subQ0])],"isStart":false})})}),makeQuery(id+"F8.opExtrude","SWEPT_FACE",FACE,{"disambiguationData":[OSD([sQuery(id+"F7.wireOp",EDGE,"E67")])]})]});}
            var Q5;
            Q5=makeQuery(id+"F8.boolean.opBoolean","INTERSECT",EDGE,{"disambiguationData":[OD(0.0)],"derivedFrom":[makeQuery(id+"F5.opExtrude","SWEPT_FACE",FACE,{"disambiguationData":[OSD([sQuery(id+"F4.wireOp",EDGE,"E30")])]}),makeQuery(id+"F8.opExtrude","SWEPT_FACE",FACE,{"disambiguationData":[OSD([sQuery(id+"F7.wireOp",EDGE,"E67")])]})]});
            fillet(context, id + "F14", {"entities" : qUnion([Q0, Q1, Q2, Q3, Q4, Q5]), "radius" : 3 * mm, "tangentPropagation" : true, "allowEdgeOverflow" : false});
        }
        {
            var Q0;
            Q0=makeQuery(id+"F1.opExtrude","CAP_EDGE",EDGE,{"disambiguationData":[OSD([sQuery(id+"F0.wireOp",EDGE,"E1.bottom")])],"isStart":false});
            fillet(context, id + "F15", {"entities" : qUnion([Q0]), "radius" : 2 * mm, "tangentPropagation" : true, "allowEdgeOverflow" : false});
        }
        {
            var Q0;
            {var subQ0=sQuery(id+"F0.wireOp",EDGE,"E21.filletArc");var subQ1=sQuery(id+"F0.wireOp",EDGE,"E7");var subQ2=sQuery(id+"F0.wireOp",EDGE,"E6");var subQ3=sQuery(id+"F0.wireOp",EDGE,"E5");var subQ4=sQuery(id+"F0.wireOp",EDGE,"E4");var subQ5=sQuery(id+"F0.wireOp",EDGE,"E22.filletArc");var subQ6=sQuery(id+"F0.wireOp",EDGE,"E1.bottom");var subQ7=sQuery(id+"F0.wireOp",EDGE,"E1.right");var subQ8=sQuery(id+"F0.wireOp",EDGE,"E1.top");var subQ9=sQuery(id+"F0.wireOp",EDGE,"E1.left");var subQ10=sQuery(id+"F0.wireOp",EDGE,"E23.filletArc");var subQ11=sQuery(id+"F0.wireOp",EDGE,"E24.filletArc");Q0=makeQuery(id+"F2.boolean.opBoolean","SPLIT",FACE,{"disambiguationData":[TD([makeQuery(id+"F1.opExtrude","SWEPT_FACE",FACE,{"disambiguationData":[OSD([subQ6])]})])],"derivedFrom":makeQuery(id+"F1.opExtrude","CAP_FACE",FACE,{"disambiguationData":[OSD([subQ6,subQ8,subQ9,subQ7,subQ4,subQ3,subQ2,subQ1,subQ0,subQ5,subQ10,subQ11])],"isStart":true})});}
            var sketch = newSketch(context, id + "F16", { "sketchPlane" : qUnion([Q0])});
            skLineSegment(sketch, "E79", {"start": v(0, 74.25) * mm, "end": v(0, 104.25) * mm, "construction": true});
            skCircle(sketch, "E80", {"center": v(0, 104.25) * mm, "radius": 6 * mm});
            skLineSegment(sketch, "E81", {"start": v(-33, 74.25) * mm, "end": v(-15, 92.25) * mm});
            skLineSegment(sketch, "E82", {"start": v(-15, 92.25) * mm, "end": v(-15, 104.25) * mm});
            skLineSegment(sketch, "E83", {"start": v(33, 74.25) * mm, "end": v(15, 92.25) * mm});
            skLineSegment(sketch, "E84", {"start": v(15, 92.25) * mm, "end": v(15, 104.25) * mm});
            skArc(sketch, "E85", {"start": v(15, 104.25) * mm, "mid": v(0, 119.25) * mm, "end": v(-15, 104.25) * mm});
            skLineSegment(sketch, "E86", {"start": v(-74.25, 0) * mm, "end": v(74.25, 0) * mm, "construction": true});
            skLineSegment(sketch, "E87.MirrorCS", {"start": v(-33, -74.25) * mm, "end": v(-15, -92.25) * mm});
            skLineSegment(sketch, "E88.MirrorCS", {"start": v(-15, -92.25) * mm, "end": v(-15, -104.25) * mm});
            skArc(sketch, "E89.MirrorCS", {"start": v(15, -104.25) * mm, "mid": v(0, -119.25) * mm, "end": v(-15, -104.25) * mm});
            skLineSegment(sketch, "E90.MirrorCS", {"start": v(15, -92.25) * mm, "end": v(15, -104.25) * mm});
            skLineSegment(sketch, "E91.MirrorCS", {"start": v(33, -74.25) * mm, "end": v(15, -92.25) * mm});
            skLineSegment(sketch, "E92.MirrorCS", {"start": v(0, -74.25) * mm, "end": v(0, -104.25) * mm, "construction": true});
            skCircle(sketch, "E93.MirrorC", {"center": v(0, -104.25) * mm, "radius": 6 * mm});
            skSolve(sketch);
        }
        {
            var Q0;
            Q0=makeQuery(id+"F16.imprint","IMPRINT",FACE,{"disambiguationData":[TD([[makeQuery(id+"F16.imprint","IMPRINT",EDGE,{"derivedFrom":sQuery(id+"F16.wireOp",EDGE,"E80")}),-1.0]])]});
            var Q1;
            Q1=makeQuery(id+"F16.imprint","IMPRINT",FACE,{"disambiguationData":[TD([[makeQuery(id+"F16.imprint","IMPRINT",EDGE,{"derivedFrom":makeQuery(id+"F1.opExtrude","CAP_EDGE",EDGE,{"disambiguationData":[OSD([sQuery(id+"F0.wireOp",EDGE,"E1.left")])],"isStart":true})}),-1.0]])]});
            var Q2;
            {var subQ0=sQuery(id+"F16.wireOp",EDGE,"E87.MirrorCS");Q2=makeQuery(id+"F16.imprint","IMPRINT",FACE,{"disambiguationData":[TD([[makeQuery(id+"F16.imprint","IMPRINT",EDGE,{"derivedFrom":subQ0}),1.0]])]});}
            var Q3;
            Q3=makeQuery(id+"F2.opExtrude","CAP_FACE",FACE,{"disambiguationData":[OSD([sQuery(id+"F0.wireOp",EDGE,"E12"),sQuery(id+"F0.wireOp",EDGE,"E13"),sQuery(id+"F0.wireOp",EDGE,"E14"),sQuery(id+"F0.wireOp",EDGE,"E15"),sQuery(id+"F0.wireOp",EDGE,"E17.filletArc"),sQuery(id+"F0.wireOp",EDGE,"E18.filletArc"),sQuery(id+"F0.wireOp",EDGE,"E19.filletArc"),sQuery(id+"F0.wireOp",EDGE,"E20.filletArc"),sQuery(id+"F0.wireOp",EDGE,"E25.0"),sQuery(id+"F0.wireOp",EDGE,"E25.1"),sQuery(id+"F0.wireOp",EDGE,"E25.2"),sQuery(id+"F0.wireOp",EDGE,"E25.3"),sQuery(id+"F0.wireOp",EDGE,"E25.4"),sQuery(id+"F0.wireOp",EDGE,"E25.5"),sQuery(id+"F0.wireOp",EDGE,"E25.6"),sQuery(id+"F0.wireOp",EDGE,"E25.7")])],"isStart":false});
            extrude(context, id + "F17", {"entities" : qUnion([Q0, Q1, Q2]), "endBound" : BoundingType.UP_TO_SURFACE, "endBoundEntityFace" : qUnion([Q3]), "depth" : 25 * mm});
        }
    });
